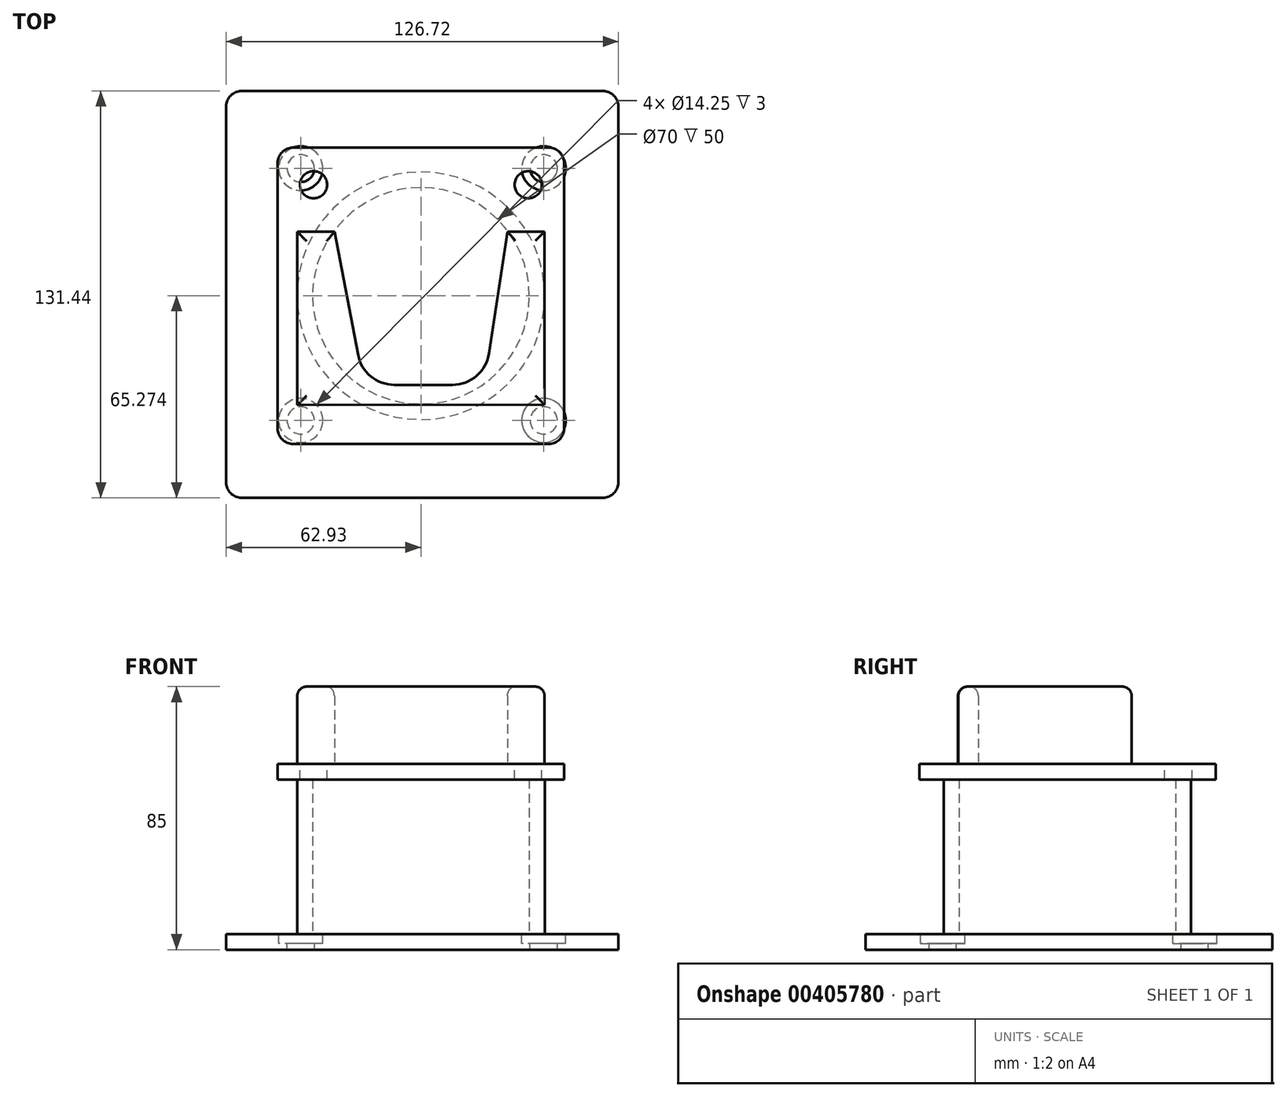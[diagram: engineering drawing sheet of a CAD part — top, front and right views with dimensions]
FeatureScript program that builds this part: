
annotation { "Feature Type Name" : "Feature", "Feature Type Description" : "" }
export const myFeature = defineFeature(function(context is Context, id is Id, definition is map)
    precondition{}
    {
        {
            var Q0;
            Q0=qCreatedBy(makeId("Top.planeOp"),FACE);
            var sketch = newSketch(context, id + "F0", { "sketchPlane" : qUnion([Q0])});
            skLineSegment(sketch, "E0.bottom", {"start": v(-62.93, 57.13) * mm, "end": v(63.79, 57.13) * mm});
            skLineSegment(sketch, "E0.top", {"start": v(-62.93, -74.3) * mm, "end": v(63.79, -74.3) * mm});
            skLineSegment(sketch, "E0.left", {"start": v(-62.93, 57.13) * mm, "end": v(-62.93, -74.3) * mm});
            skLineSegment(sketch, "E0.right", {"start": v(63.79, 57.13) * mm, "end": v(63.79, -74.3) * mm});
            skSolve(sketch);
        }
        {
            var Q0;
            Q0=makeQuery(id+"F0.imprint","IMPRINT",FACE,{"disambiguationData":[TD([[makeQuery(id+"F0.imprint","IMPRINT",EDGE,{"derivedFrom":sQuery(id+"F0.wireOp",EDGE,"E0.bottom")}),-1.0]])]});
            extrude(context, id + "F1", {"entities" : qUnion([Q0]), "depth" : 5 * mm});
        }
        {
            var Q0;
            Q0=makeQuery(id+"F1.opExtrude","CAP_FACE",FACE,{"disambiguationData":[OSD([sQuery(id+"F0.wireOp",EDGE,"E0.bottom"),sQuery(id+"F0.wireOp",EDGE,"E0.top"),sQuery(id+"F0.wireOp",EDGE,"E0.left"),sQuery(id+"F0.wireOp",EDGE,"E0.right")])],"isStart":false});
            var sketch = newSketch(context, id + "F2", { "sketchPlane" : qUnion([Q0])});
            skLineSegment(sketch, "E1", {"start": v(-62.93, 57.13) * mm, "end": v(-27.31, 20.19) * mm});
            skLineSegment(sketch, "E2", {"start": v(63.79, -74.3) * mm, "end": v(63.79, 57.13) * mm});
            skLineSegment(sketch, "E3", {"start": v(63.79, 57.13) * mm, "end": v(27.76, 19.76) * mm});
            skLineSegment(sketch, "E4", {"start": v(-62.93, -74.3) * mm, "end": v(-62.93, 57.13) * mm});
            skLineSegment(sketch, "E5.0", {"start": v(-62.93, 62.13) * mm, "end": v(63.79, 62.13) * mm});
            skLineSegment(sketch, "E6.0", {"start": v(-62.93, 32.13) * mm, "end": v(-38.82, 32.13) * mm});
            skLineSegment(sketch, "E7.0", {"start": v(-62.93, -49.3) * mm, "end": v(-38.82, -49.3) * mm});
            skLineSegment(sketch, "E8.trimOffspring", {"start": v(39.68, 32.13) * mm, "end": v(63.79, 32.13) * mm});
            skLineSegment(sketch, "E9.trimOffspring", {"start": v(39.68, -49.3) * mm, "end": v(63.79, -49.3) * mm});
            skCircle(sketch, "E10", {"center": v(0, -9.04) * mm, "radius": 40 * mm});
            skLineSegment(sketch, "E11.trimOffspring", {"start": v(28.2, -37.4) * mm, "end": v(63.79, -74.3) * mm});
            skLineSegment(sketch, "E12.trimOffspring", {"start": v(-27.76, -37.83) * mm, "end": v(-62.93, -74.3) * mm});
            skCircle(sketch, "E13", {"center": v(0, -9.04) * mm, "radius": 35 * mm});
            skSolve(sketch);
        }
        {
            var Q0;
            Q0=sQuery(id+"F2.wireOp",VERTEX,"E6.0.end");
            var Q1;
            Q1=sQuery(id+"F2.wireOp",VERTEX,"E8.trimOffspring.start");
            var Q2;
            Q2=sQuery(id+"F2.wireOp",VERTEX,"E9.trimOffspring.start");
            var Q3;
            Q3=sQuery(id+"F2.wireOp",VERTEX,"E7.0.end");
            var Q4;
            Q4=makeQuery(id+"F1.opExtrude","SWEPT_BODY",BODY,{"disambiguationData":[OSD([sQuery(id+"F0.wireOp",EDGE,"E0.bottom"),sQuery(id+"F0.wireOp",EDGE,"E0.top"),sQuery(id+"F0.wireOp",EDGE,"E0.left"),sQuery(id+"F0.wireOp",EDGE,"E0.right")])]});
            hole(context, id + "F3", {"style" : HoleStyle.C_BORE, "endStyle" : HoleEndStyle.THROUGH, "holeDiameter" : 8.8 * mm, "cBoreDiameter" : 14.25 * mm, "cBoreDepth" : 3 * mm, "tappedDepth" : 12 * mm, "tapClearance" : 3, "locations" : qUnion([Q0, Q1, Q2, Q3]), "scope" : qUnion([Q4])});
        }
        {
            var Q0;
            Q0=makeQuery(id+"F2.imprint","IMPRINT",FACE,{"disambiguationData":[TD([[makeQuery(id+"F2.imprint","IMPRINT",EDGE,{"derivedFrom":sQuery(id+"F2.wireOp",EDGE,"E13")}),-1.0]])]});
            extrude(context, id + "F4", {"entities" : qUnion([Q0]), "operationType" : NewBodyOperationType.ADD, "depth" : 50 * mm});
        }
        {
            var Q0;
            Q0=makeQuery(id+"F4.opExtrude","CAP_FACE",FACE,{"disambiguationData":[OSD([sQuery(id+"F2.wireOp",EDGE,"E10"),sQuery(id+"F2.wireOp",EDGE,"E13")])],"isStart":false});
            var sketch = newSketch(context, id + "F5", { "sketchPlane" : qUnion([Q0])});
            skLineSegment(sketch, "E14.bottom", {"start": v(-46.3, 38.84) * mm, "end": v(46.3, 38.84) * mm});
            skLineSegment(sketch, "E14.top", {"start": v(-46.3, -56.91) * mm, "end": v(46.3, -56.91) * mm});
            skLineSegment(sketch, "E14.left", {"start": v(-46.3, 38.84) * mm, "end": v(-46.3, -56.91) * mm});
            skLineSegment(sketch, "E14.right", {"start": v(46.3, 38.84) * mm, "end": v(46.3, -56.91) * mm});
            skPoint(sketch, "E14.middle", {"position": v(0, -9.04) * mm});
            skSolve(sketch);
        }
        {
            var Q0;
            Q0=makeQuery(id+"F5.imprint","IMPRINT",FACE,{"disambiguationData":[TD([[makeQuery(id+"F5.imprint","IMPRINT",EDGE,{"derivedFrom":sQuery(id+"F5.wireOp",EDGE,"E14.bottom")}),-1.0]])]});
            var sketch = newSketch(context, id + "F6", { "sketchPlane" : qUnion([Q0])});
            skSolve(sketch);
        }
        {
            var Q0;
            Q0 = qSketchRegion(id + "F6", true);
            var Q1;
            Q1=makeQuery(id+"F5.imprint","IMPRINT",FACE,{"disambiguationData":[TD([[makeQuery(id+"F5.imprint","IMPRINT",EDGE,{"derivedFrom":sQuery(id+"F5.wireOp",EDGE,"E14.bottom")}),-1.0]])]});
            var Q2;
            Q2=makeQuery(id+"F5.imprint","IMPRINT",FACE,{"disambiguationData":[TD([[makeQuery(id+"F5.imprint","IMPRINT",EDGE,{"derivedFrom":makeQuery(id+"F4.opExtrude","CAP_EDGE",EDGE,{"disambiguationData":[OSD([sQuery(id+"F2.wireOp",EDGE,"E10")])],"isStart":false})}),1.0]])]});
            var Q3;
            Q3=makeQuery(id+"F5.imprint","IMPRINT",FACE,{"disambiguationData":[TD([[makeQuery(id+"F5.imprint","IMPRINT",EDGE,{"derivedFrom":makeQuery(id+"F4.opExtrude","CAP_EDGE",EDGE,{"disambiguationData":[OSD([sQuery(id+"F2.wireOp",EDGE,"E13")])],"isStart":false})}),1.0]])]});
            extrude(context, id + "F7", {"entities" : qUnion([Q0, Q1, Q2, Q3]), "operationType" : NewBodyOperationType.ADD, "depth" : 5 * mm});
        }
        {
            var Q0;
            Q0=makeQuery(id+"F7.opExtrude","CAP_FACE",FACE,{"disambiguationData":[OSD([sQuery(id+"F5.wireOp",EDGE,"E14.bottom"),sQuery(id+"F5.wireOp",EDGE,"E14.top"),sQuery(id+"F5.wireOp",EDGE,"E14.left"),sQuery(id+"F5.wireOp",EDGE,"E14.right")])],"isStart":false});
            var sketch = newSketch(context, id + "F8", { "sketchPlane" : qUnion([Q0])});
            skPoint(sketch, "E15.orphan", {"position": v(-16.69, -22.82) * mm});
            skPoint(sketch, "E16.orphan", {"position": v(-25, 12.18) * mm});
            skPoint(sketch, "E17.orphan", {"position": v(25, 12.18) * mm});
            skPoint(sketch, "E18.orphan", {"position": v(25, -34.82) * mm});
            skPoint(sketch, "E19.orphan", {"position": v(-25, -34.82) * mm});
            skPoint(sketch, "E20.visualSharp", {"position": v(-15.98, -34.82) * mm});
            skPoint(sketch, "E21.visualSharp", {"position": v(17.9, -34.82) * mm});
            skLineSegment(sketch, "E22.0", {"start": v(27.97, 11.73) * mm, "end": v(22.03, -27.61) * mm});
            skArc(sketch, "E23.0", {"start": v(10.16, -37.82) * mm, "mid": v(17.99, -34.92) * mm, "end": v(22.03, -27.61) * mm});
            skLineSegment(sketch, "E24.0", {"start": v(0, -37.82) * mm, "end": v(10.16, -37.82) * mm});
            skLineSegment(sketch, "E25.0", {"start": v(0, -37.82) * mm, "end": v(-8.54, -37.82) * mm});
            skArc(sketch, "E26.0", {"start": v(-20.33, -28.08) * mm, "mid": v(-16.19, -35.07) * mm, "end": v(-8.54, -37.82) * mm});
            skLineSegment(sketch, "E27.0", {"start": v(-27.95, 11.61) * mm, "end": v(-20.33, -28.08) * mm});
            skLineSegment(sketch, "E28", {"start": v(-27.95, 11.61) * mm, "end": v(-39.95, 11.61) * mm});
            skLineSegment(sketch, "E29", {"start": v(-39.95, 11.61) * mm, "end": v(-39.95, -44.39) * mm});
            skLineSegment(sketch, "E30", {"start": v(27.97, 11.73) * mm, "end": v(39.97, 11.73) * mm});
            skLineSegment(sketch, "E31", {"start": v(39.97, 11.73) * mm, "end": v(39.97, -44.27) * mm});
            skLineSegment(sketch, "E32", {"start": v(39.97, -44.27) * mm, "end": v(-39.95, -44.39) * mm});
            skLineSegment(sketch, "E33.0", {"start": v(-46.3, 26.84) * mm, "end": v(-34.7, 26.84) * mm});
            skLineSegment(sketch, "E34.trimOffspring", {"start": v(34.7, 26.84) * mm, "end": v(46.3, 26.84) * mm});
            skSolve(sketch);
        }
        {
            var Q0;
            Q0=makeQuery(id+"F8.imprint","IMPRINT",FACE,{"disambiguationData":[TD([[makeQuery(id+"F8.imprint","IMPRINT",EDGE,{"derivedFrom":sQuery(id+"F8.wireOp",EDGE,"E22.0")}),1.0]])]});
            extrude(context, id + "F9", {"entities" : qUnion([Q0]), "operationType" : NewBodyOperationType.ADD, "depth" : 18 * mm});
        }
        {
            var Q0;
            Q0 = qSketchRegion(id + "F8", true);
            extrude(context, id + "F10", {"entities" : qUnion([Q0]), "operationType" : NewBodyOperationType.ADD, "depth" : 25 * mm});
        }
        {
            var Q0;
            Q0=sQuery(id+"F8.wireOp",VERTEX,"E33.0.end");
            var Q1;
            Q1=sQuery(id+"F8.wireOp",VERTEX,"E34.trimOffspring.start");
            var Q2;
            Q2=makeQuery(id+"F1.opExtrude","SWEPT_BODY",BODY,{"disambiguationData":[OSD([sQuery(id+"F0.wireOp",EDGE,"E0.bottom"),sQuery(id+"F0.wireOp",EDGE,"E0.top"),sQuery(id+"F0.wireOp",EDGE,"E0.left"),sQuery(id+"F0.wireOp",EDGE,"E0.right")])]});
            hole(context, id + "F11", {"style" : HoleStyle.SIMPLE, "endStyle" : HoleEndStyle.BLIND, "holeDiameter" : 8.8 * mm, "holeDepth" : 20 * mm, "tappedDepth" : 12 * mm, "tapClearance" : 3, "locations" : qUnion([Q0, Q1]), "scope" : qUnion([Q2])});
        }
        {
            var Q0;
            Q0=makeQuery(id+"F4.opExtrude","CAP_EDGE",EDGE,{"disambiguationData":[OSD([sQuery(id+"F2.wireOp",EDGE,"E10")])],"isStart":true});
            var Q1;
            Q1=makeQuery(id+"F9.opExtrude","CAP_EDGE",EDGE,{"disambiguationData":[OSD([sQuery(id+"F8.wireOp",EDGE,"E32")])],"isStart":true});
            var Q2;
            Q2=makeQuery(id+"F9.opExtrude","CAP_EDGE",EDGE,{"disambiguationData":[OSD([sQuery(id+"F8.wireOp",EDGE,"E31")])],"isStart":true});
            var Q3;
            Q3=makeQuery(id+"F9.opExtrude","CAP_EDGE",EDGE,{"disambiguationData":[OSD([sQuery(id+"F8.wireOp",EDGE,"E30")])],"isStart":true});
            var Q4;
            Q4=makeQuery(id+"F9.opExtrude","CAP_EDGE",EDGE,{"disambiguationData":[OSD([sQuery(id+"F8.wireOp",EDGE,"E28")])],"isStart":true});
            var Q5;
            Q5=makeQuery(id+"F9.opExtrude","CAP_EDGE",EDGE,{"disambiguationData":[OSD([sQuery(id+"F8.wireOp",EDGE,"E29")])],"isStart":true});
            var Q6;
            Q6=makeQuery(id+"F9.opExtrude","CAP_EDGE",EDGE,{"disambiguationData":[OSD([sQuery(id+"F8.wireOp",EDGE,"E27.0")])],"isStart":true});
            var Q7;
            Q7=makeQuery(id+"F10.opExtrude","CAP_EDGE",EDGE,{"disambiguationData":[OSD([sQuery(id+"F8.wireOp",EDGE,"E23.0")])],"isStart":false});
            var Q8;
            Q8=makeQuery(id+"F10.opExtrude","CAP_EDGE",EDGE,{"disambiguationData":[OSD([sQuery(id+"F8.wireOp",EDGE,"E31")])],"isStart":false});
            var Q9;
            Q9=makeQuery(id+"F10.opExtrude","CAP_EDGE",EDGE,{"disambiguationData":[OSD([sQuery(id+"F8.wireOp",EDGE,"E32")])],"isStart":false});
            var Q10;
            Q10=makeQuery(id+"F10.opExtrude","CAP_EDGE",EDGE,{"disambiguationData":[OSD([sQuery(id+"F8.wireOp",EDGE,"E29")])],"isStart":false});
            var Q11;
            Q11=makeQuery(id+"F10.opExtrude","CAP_EDGE",EDGE,{"disambiguationData":[OSD([sQuery(id+"F8.wireOp",EDGE,"E28")])],"isStart":false});
            var Q12;
            Q12=makeQuery(id+"F10.opExtrude","CAP_EDGE",EDGE,{"disambiguationData":[OSD([sQuery(id+"F8.wireOp",EDGE,"E30")])],"isStart":false});
            var Q13;
            Q13=makeQuery(id+"F4.opExtrude","CAP_EDGE",EDGE,{"disambiguationData":[OSD([sQuery(id+"F2.wireOp",EDGE,"E10")])],"isStart":false});
            fillet(context, id + "F12", {"entities" : qUnion([Q0, Q1, Q2, Q3, Q4, Q5, Q6, Q7, Q8, Q9, Q10, Q11, Q12, Q13]), "radius" : 3 * mm, "tangentPropagation" : true, "allowEdgeOverflow" : false});
        }
        {
            var Q0;
            Q0=makeQuery(id+"F1.opExtrude","SWEPT_EDGE",EDGE,{"disambiguationData":[OSD([sQuery(id+"F0.wireOp",EDGE,"E0.bottom"),sQuery(id+"F0.wireOp",EDGE,"E0.right")])]});
            var Q1;
            Q1=makeQuery(id+"F1.opExtrude","SWEPT_EDGE",EDGE,{"disambiguationData":[OSD([sQuery(id+"F0.wireOp",EDGE,"E0.bottom"),sQuery(id+"F0.wireOp",EDGE,"E0.left")])]});
            var Q2;
            Q2=makeQuery(id+"F1.opExtrude","SWEPT_EDGE",EDGE,{"disambiguationData":[OSD([sQuery(id+"F0.wireOp",EDGE,"E0.top"),sQuery(id+"F0.wireOp",EDGE,"E0.right")])]});
            var Q3;
            Q3=makeQuery(id+"F7.opExtrude","SWEPT_EDGE",EDGE,{"disambiguationData":[OSD([sQuery(id+"F5.wireOp",EDGE,"E14.top"),sQuery(id+"F5.wireOp",EDGE,"E14.right")])]});
            var Q4;
            Q4=makeQuery(id+"F7.opExtrude","SWEPT_EDGE",EDGE,{"disambiguationData":[OSD([sQuery(id+"F5.wireOp",EDGE,"E14.bottom"),sQuery(id+"F5.wireOp",EDGE,"E14.right")])]});
            var Q5;
            Q5=makeQuery(id+"F7.opExtrude","SWEPT_EDGE",EDGE,{"disambiguationData":[OSD([sQuery(id+"F5.wireOp",EDGE,"E14.bottom"),sQuery(id+"F5.wireOp",EDGE,"E14.left")])]});
            var Q6;
            Q6=makeQuery(id+"F1.opExtrude","SWEPT_EDGE",EDGE,{"disambiguationData":[OSD([sQuery(id+"F0.wireOp",EDGE,"E0.top"),sQuery(id+"F0.wireOp",EDGE,"E0.left")])]});
            var Q7;
            Q7=makeQuery(id+"F7.opExtrude","SWEPT_EDGE",EDGE,{"disambiguationData":[OSD([sQuery(id+"F5.wireOp",EDGE,"E14.top"),sQuery(id+"F5.wireOp",EDGE,"E14.left")])]});
            fillet(context, id + "F13", {"entities" : qUnion([Q0, Q1, Q2, Q3, Q4, Q5, Q6, Q7]), "radius" : 5 * mm, "tangentPropagation" : true, "allowEdgeOverflow" : false});
        }
    });
